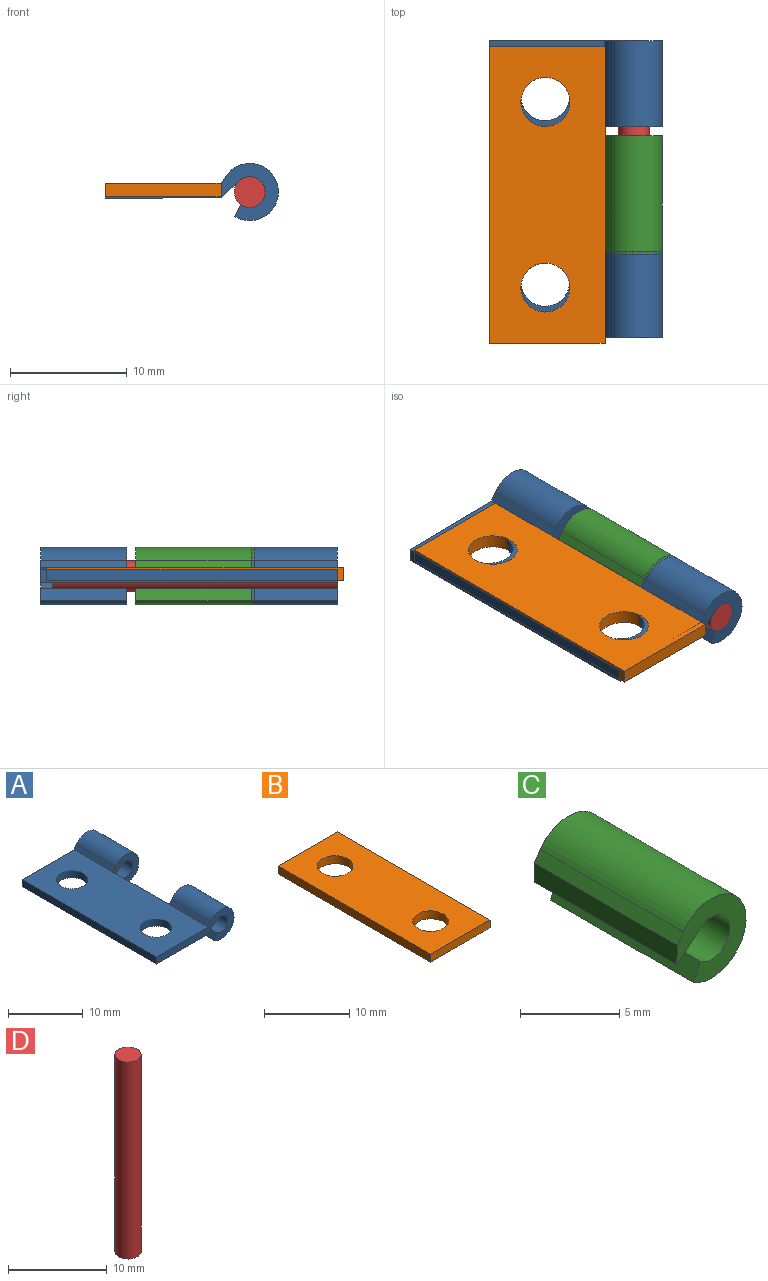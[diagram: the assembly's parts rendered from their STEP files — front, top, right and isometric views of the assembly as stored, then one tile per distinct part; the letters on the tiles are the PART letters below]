
ASSEMBLY  parts=4 mates=3
PART A: 20 faces, bbox 14.8x25.4x4.9 mm
  f0: plane 10.67x1.14mm, normal (1,0,0), area 12.2mm2, adj f6,f7,f13,f19
  f1: plane 14.77x4.9mm, normal (0,1,0), area 22.5mm2, adj f2,f6,f7,f8,f9,f10,f11,f12
  f2: plane 25.4x1.14mm, normal (-1,0,0), area 29mm2, adj f1,f4,f6,f7
  f3: cylinder r=2.1mm len=4.19mm, axis (0,0,-1), area 15mm2, adj f6,f7
  f4: plane 14.77x4.9mm, normal (0,-1,0), area 22.5mm2, adj f2,f6,f7,f14,f15,f16,f17,f18
  f5: cylinder r=2.1mm len=4.19mm, axis (0,0,-1), area 15mm2, adj f6,f7
  f6: plane 25.4x9.86mm, normal (0,0,1), area 222.7mm2, adj f0,f1,f2,f3,f4,f5,f9,f18
  f7: plane 25.4x9.86mm, normal (0,0,-1), area 222.7mm2, adj f0,f1,f2,f3,f4,f5,f8,f14
  f8: plane 7.37x1.61mm, normal (0.65,0,-0.76), area 15.7mm2, adj f1,f7,f12,f13
  f9: plane 7.37x0.65mm, normal (-0.82,0,0.57), area 5.8mm2, adj f1,f6,f10,f13
  f10: cylinder r=2.45mm len=7.37mm, axis (0,1,0), area 84.2mm2, adj f1,f9,f11,f13
  f11: plane 7.37x1.03mm, normal (-0.89,0,0.45), area 8.5mm2, adj f1,f10,f12,f13
  f12: cylinder r=1.31mm len=7.37mm, axis (0,1,0), area 43.3mm2, adj f1,f8,f11,f13
  f13: plane 4.92x4.9mm, normal (0,-1,0), area 11.3mm2, adj f0,f8,f9,f10,f11,f12
  f14: plane 7.37x1.61mm, normal (0.65,0,-0.76), area 15.7mm2, adj f4,f7,f15,f19
  f15: cylinder r=1.31mm len=7.37mm, axis (0,-1,0), area 43.3mm2, adj f4,f14,f16,f19
  f16: plane 7.37x1.03mm, normal (-0.89,0,0.45), area 8.5mm2, adj f4,f15,f17,f19
  f17: cylinder r=2.45mm len=7.37mm, axis (0,-1,0), area 84.2mm2, adj f4,f16,f18,f19
  f18: plane 7.37x0.65mm, normal (-0.82,0,0.57), area 5.8mm2, adj f4,f6,f17,f19
  f19: plane 4.92x4.9mm, normal (0,1,0), area 11.3mm2, adj f0,f14,f15,f16,f17,f18
PART B: 8 faces, bbox 9.9x25.4x1.1 mm
  f0: plane 25.4x1.14mm, normal (-1,0,0), area 29mm2, adj f1,f4,f6,f7
  f1: plane 9.86x1.14mm, normal (0,-1,0), area 11.3mm2, adj f0,f2,f6,f7
  f2: plane 25.4x1.14mm, normal (1,0,0), area 29mm2, adj f1,f4,f6,f7
  f3: cylinder r=2.1mm len=4.19mm, axis (0,0,-1), area 15mm2, adj f6,f7
  f4: plane 9.86x1.14mm, normal (0,1,0), area 11.3mm2, adj f0,f2,f6,f7
  f5: cylinder r=2.1mm len=4.19mm, axis (0,0,-1), area 15mm2, adj f6,f7
  f6: plane 25.4x9.86mm, normal (0,0,1), area 222.7mm2, adj f0,f1,f2,f3,f4,f5
  f7: plane 25.4x9.86mm, normal (0,0,-1), area 222.7mm2, adj f0,f1,f2,f3,f4,f5
PART C: 9 faces, bbox 4.9x10.2x4.9 mm
  f0: plane 10.16x0.62mm, normal (-0.82,0,0.57), area 7.7mm2, adj f1,f6,f7,f8
  f1: plane 10.16x1.17mm, normal (-1,0,0.02), area 11.8mm2, adj f0,f2,f7,f8
  f2: cylinder r=0.06mm len=10.16mm, axis (0,-1,0), area 0.2mm2, adj f1,f3,f7,f8
  f3: plane 10.16x1.59mm, normal (0.65,0,-0.76), area 21.4mm2, adj f2,f4,f7,f8
  f4: cylinder r=1.31mm len=10.16mm, axis (0,-1,0), area 59.7mm2, adj f3,f5,f7,f8
  f5: plane 10.16x1.03mm, normal (-0.89,0,0.45), area 11.7mm2, adj f4,f6,f7,f8
  f6: cylinder r=2.45mm len=10.16mm, axis (0,-1,0), area 116.1mm2, adj f0,f5,f7,f8
  f7: plane 4.92x4.9mm, normal (0,1,0), area 11.3mm2, adj f0,f1,f2,f3,f4,f5,f6
  f8: plane 4.92x4.9mm, normal (0,-1,0), area 11.3mm2, adj f0,f1,f2,f3,f4,f5,f6
PART D: 3 faces, bbox 2.6x2.6x24.4 mm
  f0: cylinder r=1.32mm len=24.4mm, axis (0,0,-1), area 202.4mm2, adj f1,f2
  f1: plane 2.64x2.64mm, normal (0,0,1), area 5.5mm2, adj f0
  f2: plane 2.64x2.64mm, normal (0,0,-1), area 5.5mm2, adj f0
PLACE A rot(axis=(0,-1,0),0.9deg) t=(24.54,36.23,-0.86)mm
PLACE B t=(24.55,-12.7,-1.14)mm
PLACE C rot(axis=(0,-1,0),0.9deg) t=(24.54,-12.7,-0.86)mm
PLACE D rot(axis=(-1,-0.01,-0.01),90deg) t=(61.69,-12.2,7.45)mm
MATE fastened D.f0 <-> A.f10  axis (0,-1,0) through (7.36,-12.2,-0.74)mm
MATE fastened B.f2 <-> C.f1  axis (1,0,0) through (4.91,-12.7,0)mm
MATE revolute D.f0 <-> C.f4  axis (0,-1,0) through (7.36,0,-0.74)mm
